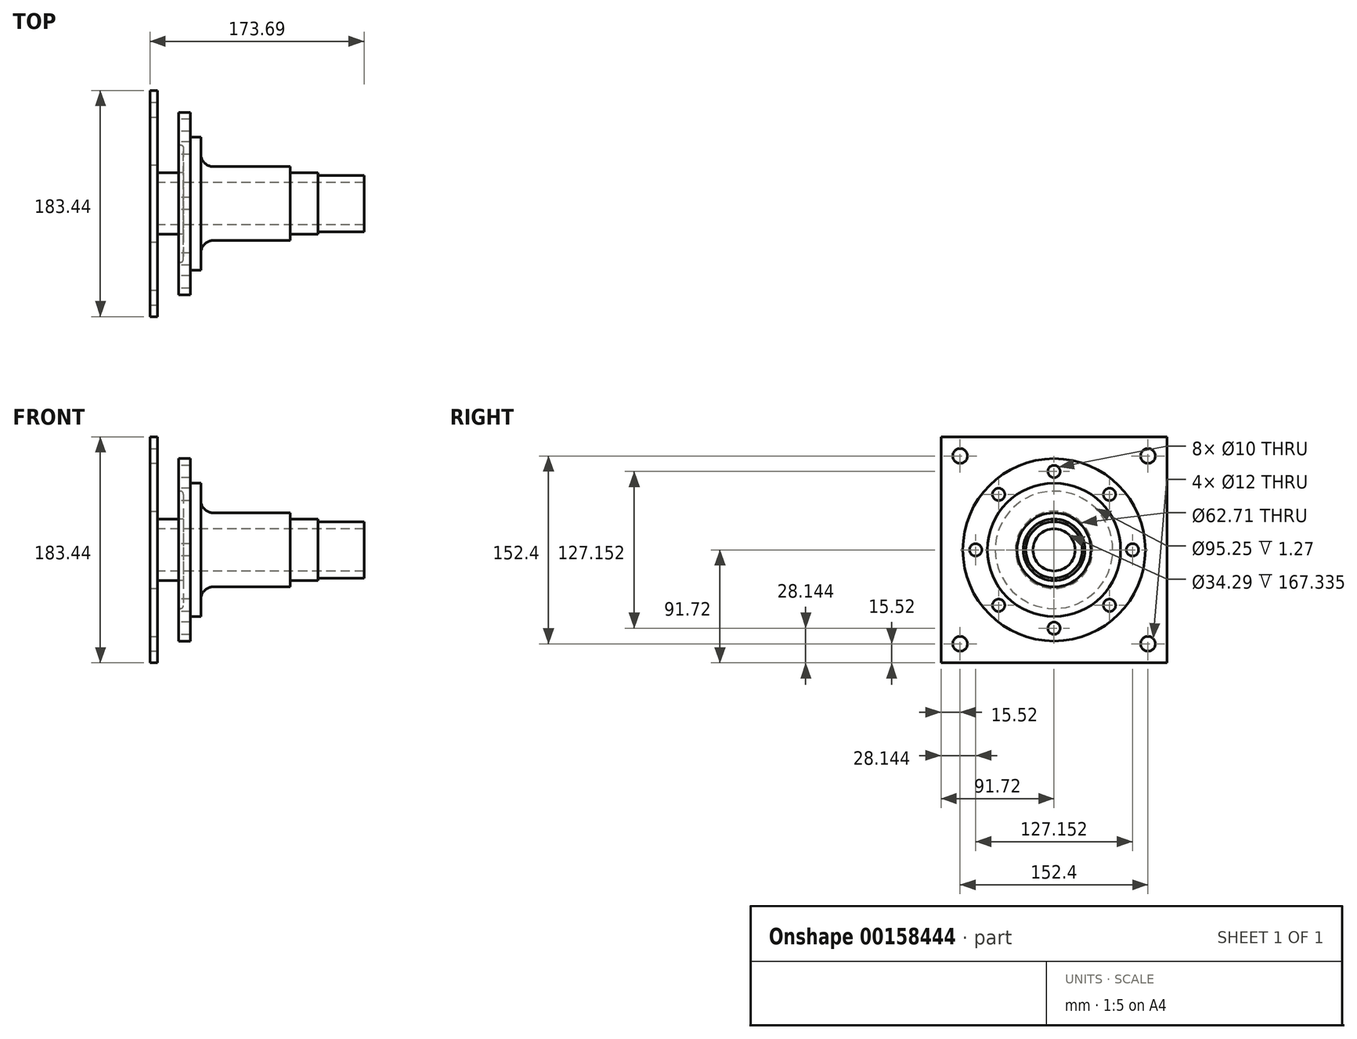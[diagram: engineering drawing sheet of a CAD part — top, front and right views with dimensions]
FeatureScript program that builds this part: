
annotation { "Feature Type Name" : "Feature", "Feature Type Description" : "" }
export const myFeature = defineFeature(function(context is Context, id is Id, definition is map)
    precondition{}
    {
        {
            var Q0;
            Q0=qCreatedBy(makeId("Front.planeOp"),FACE);
            var sketch = newSketch(context, id + "F0", { "sketchPlane" : qUnion([Q0])});
            skLineSegment(sketch, "E0", {"start": v(0, 17.15) * mm, "end": v(0, 25) * mm});
            skLineSegment(sketch, "E1", {"start": v(0, 25) * mm, "end": v(20.9, 25) * mm});
            skLineSegment(sketch, "E2", {"start": v(20.9, 25) * mm, "end": v(20.9, 45.09) * mm});
            skLineSegment(sketch, "E3", {"start": v(18.36, 47.63) * mm, "end": v(17.1, 47.63) * mm});
            skLineSegment(sketch, "E4", {"start": v(17.1, 47.63) * mm, "end": v(17.1, 74) * mm});
            skLineSegment(sketch, "E5", {"start": v(17.1, 74) * mm, "end": v(26.62, 74) * mm});
            skLineSegment(sketch, "E6", {"start": v(26.62, 74) * mm, "end": v(26.62, 54) * mm});
            skLineSegment(sketch, "E7", {"start": v(26.62, 54) * mm, "end": v(35, 54) * mm});
            skLineSegment(sketch, "E8", {"start": v(35, 54) * mm, "end": v(35, 40.16) * mm});
            skLineSegment(sketch, "E9", {"start": v(45.16, 30) * mm, "end": v(107.4, 30) * mm});
            skLineSegment(sketch, "E10", {"start": v(107.4, 30) * mm, "end": v(107.4, 25) * mm});
            skLineSegment(sketch, "E11", {"start": v(107.4, 25) * mm, "end": v(130, 25) * mm});
            skLineSegment(sketch, "E12", {"start": v(130, 25) * mm, "end": v(130, 22.87) * mm});
            skLineSegment(sketch, "E13", {"start": v(130, 22.87) * mm, "end": v(167.34, 22.87) * mm});
            skLineSegment(sketch, "E14", {"start": v(167.34, 22.87) * mm, "end": v(167.34, 17.15) * mm});
            skLineSegment(sketch, "E15", {"start": v(167.34, 17.15) * mm, "end": v(0, 17.15) * mm});
            skPoint(sketch, "E16.visualSharp", {"position": v(35, 30) * mm});
            skArc(sketch, "E16.filletArc", {"start": v(35, 40.16) * mm, "mid": v(37.98, 32.97) * mm, "end": v(45.16, 30) * mm});
            skLineSegment(sketch, "E17", {"start": v(0, 0) * mm, "end": v(167.34, 0) * mm, "construction": true});
            skPoint(sketch, "E18.visualSharp", {"position": v(20.9, 47.63) * mm});
            skArc(sketch, "E18.filletArc", {"start": v(20.9, 45.09) * mm, "mid": v(20.16, 46.88) * mm, "end": v(18.36, 47.63) * mm});
            skSolve(sketch);
        }
        {
            var Q0;
            Q0=makeQuery(id+"F0.imprint","IMPRINT",FACE,{"disambiguationData":[TD([[makeQuery(id+"F0.imprint","IMPRINT",EDGE,{"derivedFrom":sQuery(id+"F0.wireOp",EDGE,"E0")}),-1.0]])]});
            var Q1;
            Q1=sQuery(id+"F0.wireOp",EDGE,"E17");
            revolve(context, id + "F1", {"entities" : qUnion([Q0]), "axis" : qUnion([Q1]), "revolveType" : RevolveType.FULL});
        }
        {
            var Q0;
            Q0=makeQuery(id+"F1.opRevolve","SWEPT_FACE",FACE,{"disambiguationData":[OSD([sQuery(id+"F0.wireOp",EDGE,"E4")])]});
            var sketch = newSketch(context, id + "F2", { "sketchPlane" : qUnion([Q0])});
            skCircle(sketch, "E19", {"center": v(0, 63.58) * mm, "radius": 5 * mm});
            skCircle(sketch, "E20.1.0", {"center": v(-44.96, 44.96) * mm, "radius": 5 * mm});
            skCircle(sketch, "E20.2.0", {"center": v(-63.58, 0) * mm, "radius": 5 * mm});
            skCircle(sketch, "E20.3.0", {"center": v(-44.96, -44.96) * mm, "radius": 5 * mm});
            skCircle(sketch, "E20.4.0", {"center": v(0, -63.58) * mm, "radius": 5 * mm});
            skCircle(sketch, "E20.5.0", {"center": v(44.96, -44.96) * mm, "radius": 5 * mm});
            skCircle(sketch, "E20.6.0", {"center": v(63.58, 0) * mm, "radius": 5 * mm});
            skCircle(sketch, "E20.7.0", {"center": v(44.96, 44.96) * mm, "radius": 5 * mm});
            skPoint(sketch, "E20.center", {"position": v(0, 0) * mm});
            skSolve(sketch);
        }
        {
            var Q0;
            Q0 = qSketchRegion(id + "F2", true);
            extrude(context, id + "F3", {"entities" : qUnion([Q0]), "operationType" : NewBodyOperationType.REMOVE, "endBound" : BoundingType.UP_TO_NEXT, "oppositeDirection" : true, "depth" : 25.4 * mm});
        }
        {
            var Q0;
            Q0=qCreatedBy(makeId("Right.planeOp"),FACE);
            var sketch = newSketch(context, id + "F4", { "sketchPlane" : qUnion([Q0])});
            skLineSegment(sketch, "E21.bottom", {"start": v(-91.73, 91.73) * mm, "end": v(91.73, 91.73) * mm});
            skLineSegment(sketch, "E21.top", {"start": v(-91.73, -91.73) * mm, "end": v(91.73, -91.73) * mm});
            skLineSegment(sketch, "E21.left", {"start": v(-91.73, 91.73) * mm, "end": v(-91.73, -91.72) * mm});
            skLineSegment(sketch, "E21.right", {"start": v(91.73, 91.73) * mm, "end": v(91.73, -91.72) * mm});
            skPoint(sketch, "E21.middle", {"position": v(0, 0) * mm});
            skCircle(sketch, "E22", {"center": v(-76.2, 76.2) * mm, "radius": 6 * mm});
            skCircle(sketch, "E23", {"center": v(-76.2, -76.2) * mm, "radius": 6 * mm});
            skCircle(sketch, "E24", {"center": v(76.2, -76.2) * mm, "radius": 6 * mm});
            skCircle(sketch, "E25", {"center": v(76.2, 76.2) * mm, "radius": 6 * mm});
            skLineSegment(sketch, "E26", {"start": v(76.2, 76.2) * mm, "end": v(-76.2, 76.2) * mm, "construction": true});
            skLineSegment(sketch, "E27", {"start": v(-76.2, 76.2) * mm, "end": v(-76.2, -76.2) * mm, "construction": true});
            skLineSegment(sketch, "E28", {"start": v(-76.2, -76.2) * mm, "end": v(76.2, -76.2) * mm, "construction": true});
            skLineSegment(sketch, "E29", {"start": v(76.2, -76.2) * mm, "end": v(76.2, 76.2) * mm, "construction": true});
            skPoint(sketch, "E30", {"position": v(0, 76.2) * mm});
            skPoint(sketch, "E31", {"position": v(-76.2, 0) * mm});
            skCircle(sketch, "E32", {"center": v(0, 0) * mm, "radius": 31.36 * mm});
            skSolve(sketch);
        }
        {
            var Q0;
            Q0 = qSketchRegion(id + "F4", true);
            extrude(context, id + "F5", {"entities" : qUnion([Q0]), "oppositeDirection" : true, "depth" : 6.35 * mm});
        }
    });
